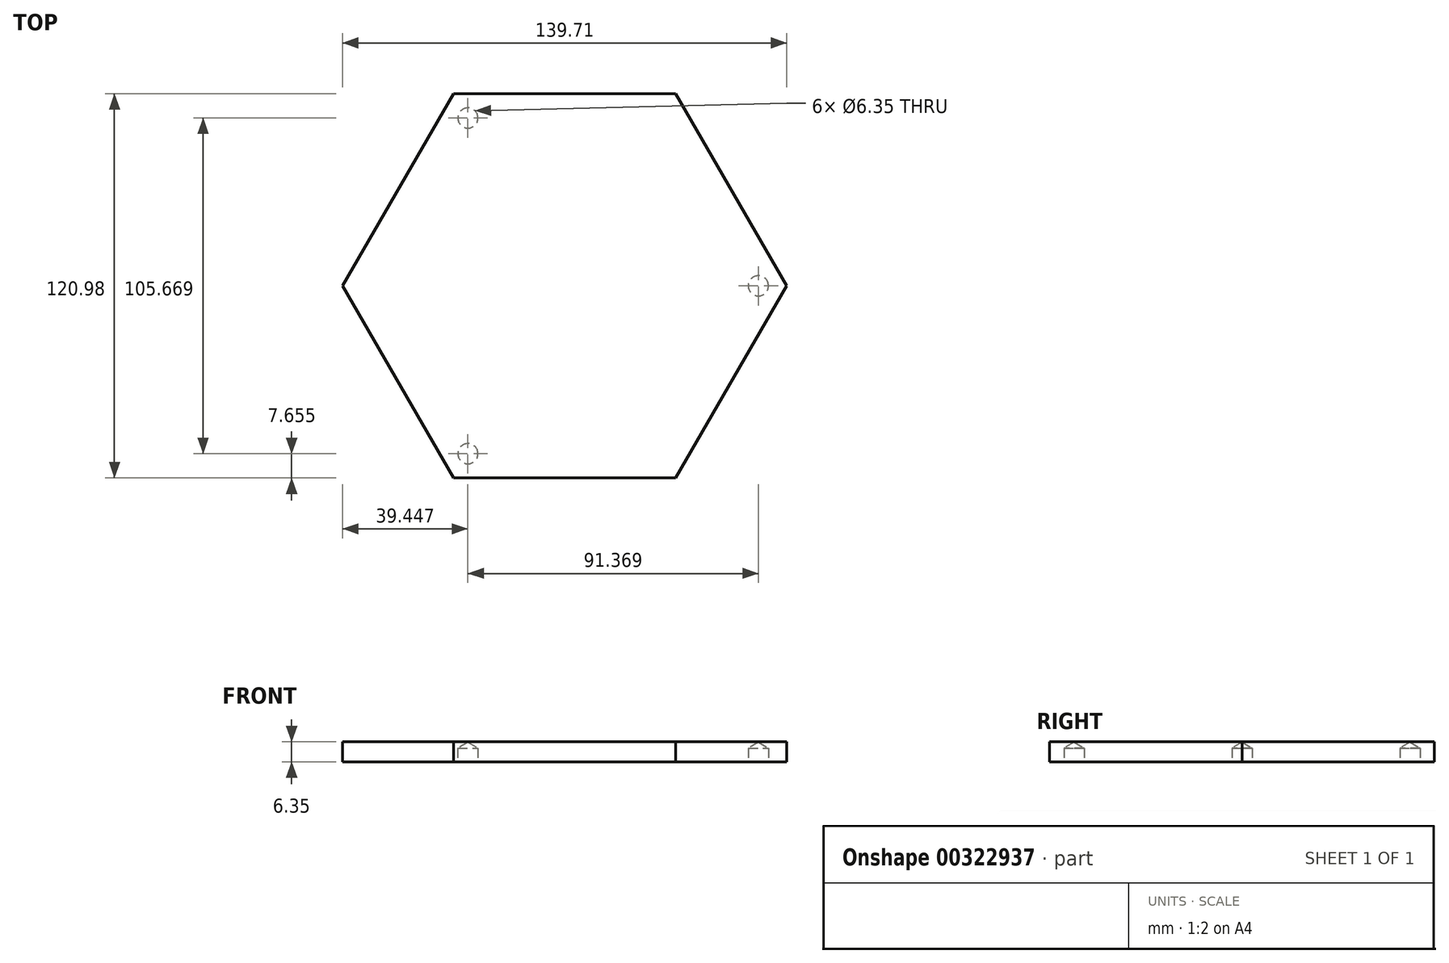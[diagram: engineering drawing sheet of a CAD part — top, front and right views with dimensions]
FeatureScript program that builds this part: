
annotation { "Feature Type Name" : "Feature", "Feature Type Description" : "" }
export const myFeature = defineFeature(function(context is Context, id is Id, definition is map)
    precondition{}
    {
        {
            var Q0;
            Q0=qCreatedBy(makeId("Top.planeOp"),FACE);
            var sketch = newSketch(context, id + "F0", { "sketchPlane" : qUnion([Q0])});
            skLineSegment(sketch, "E0.0", {"start": v(-31.75, 66) * mm, "end": v(38.1, 66) * mm});
            skLineSegment(sketch, "E0.1", {"start": v(38.1, 66) * mm, "end": v(73.02, 5.5) * mm});
            skLineSegment(sketch, "E0.2", {"start": v(73.03, 5.5) * mm, "end": v(38.1, -55) * mm});
            skLineSegment(sketch, "E0.3", {"start": v(38.1, -55) * mm, "end": v(-31.75, -55) * mm});
            skLineSegment(sketch, "E0.4", {"start": v(-31.75, -55) * mm, "end": v(-66.68, 5.5) * mm});
            skLineSegment(sketch, "E0.5", {"start": v(-66.67, 5.5) * mm, "end": v(-31.75, 66) * mm});
            skPoint(sketch, "E1", {"position": v(-41.27, 5.5) * mm});
            skPoint(sketch, "E2", {"position": v(-18.85, -33.11) * mm});
            skPoint(sketch, "E3", {"position": v(25.2, 44.11) * mm});
            skPoint(sketch, "E4", {"position": v(-18.57, 44.28) * mm});
            skPoint(sketch, "E5", {"position": v(47.62, 5.5) * mm});
            skPoint(sketch, "E6", {"position": v(25.2, -33.11) * mm});
            skPoint(sketch, "E7", {"position": v(-31.75, 66) * mm});
            skPoint(sketch, "E8", {"position": v(-27.23, 58.33) * mm});
            skPoint(sketch, "E9", {"position": v(-27.23, -47.34) * mm});
            skPoint(sketch, "E10", {"position": v(64.13, 5.5) * mm});
            skPoint(sketch, "E11", {"position": v(0, 0) * mm});
            skPoint(sketch, "E12", {"position": v(-12.7, 22.25) * mm});
            skPoint(sketch, "E13", {"position": v(-3.32, 5.66) * mm});
            skPoint(sketch, "E14", {"position": v(19.05, 22.25) * mm});
            skPoint(sketch, "E15", {"position": v(-12.7, -10.92) * mm});
            skPoint(sketch, "E16", {"position": v(19.05, -10.92) * mm});
            skSolve(sketch);
        }
        {
            var Q0;
            Q0=makeQuery(id+"F0.imprint","IMPRINT",FACE,{"disambiguationData":[TD([[makeQuery(id+"F0.imprint","IMPRINT",EDGE,{"derivedFrom":sQuery(id+"F0.wireOp",EDGE,"E0.0")}),-1.0]])]});
            extrude(context, id + "F1", {"entities" : qUnion([Q0]), "depth" : 6.35 * mm});
        }
        {
            var Q0;
            Q0=sQuery(id+"F0.wireOp",VERTEX,"E8");
            var Q1;
            Q1=sQuery(id+"F0.wireOp",VERTEX,"E9");
            var Q2;
            Q2=sQuery(id+"F0.wireOp",VERTEX,"E10");
            var Q3;
            Q3=makeQuery(id+"F1.opExtrude","SWEPT_BODY",BODY,{"disambiguationData":[OSD([sQuery(id+"F0.wireOp",EDGE,"E0.0"),sQuery(id+"F0.wireOp",EDGE,"E0.1"),sQuery(id+"F0.wireOp",EDGE,"E0.2"),sQuery(id+"F0.wireOp",EDGE,"E0.3"),sQuery(id+"F0.wireOp",EDGE,"E0.4"),sQuery(id+"F0.wireOp",EDGE,"E0.5")])]});
            hole(context, id + "F2", {"style" : HoleStyle.SIMPLE, "endStyle" : HoleEndStyle.BLIND, "oppositeDirection" : true, "holeDiameter" : 6.35 * mm, "holeDepth" : 4.32 * mm, "tappedDepth" : 12.7 * mm, "tapClearance" : 3, "locations" : qUnion([Q0, Q1, Q2]), "scope" : qUnion([Q3])});
        }
    });
